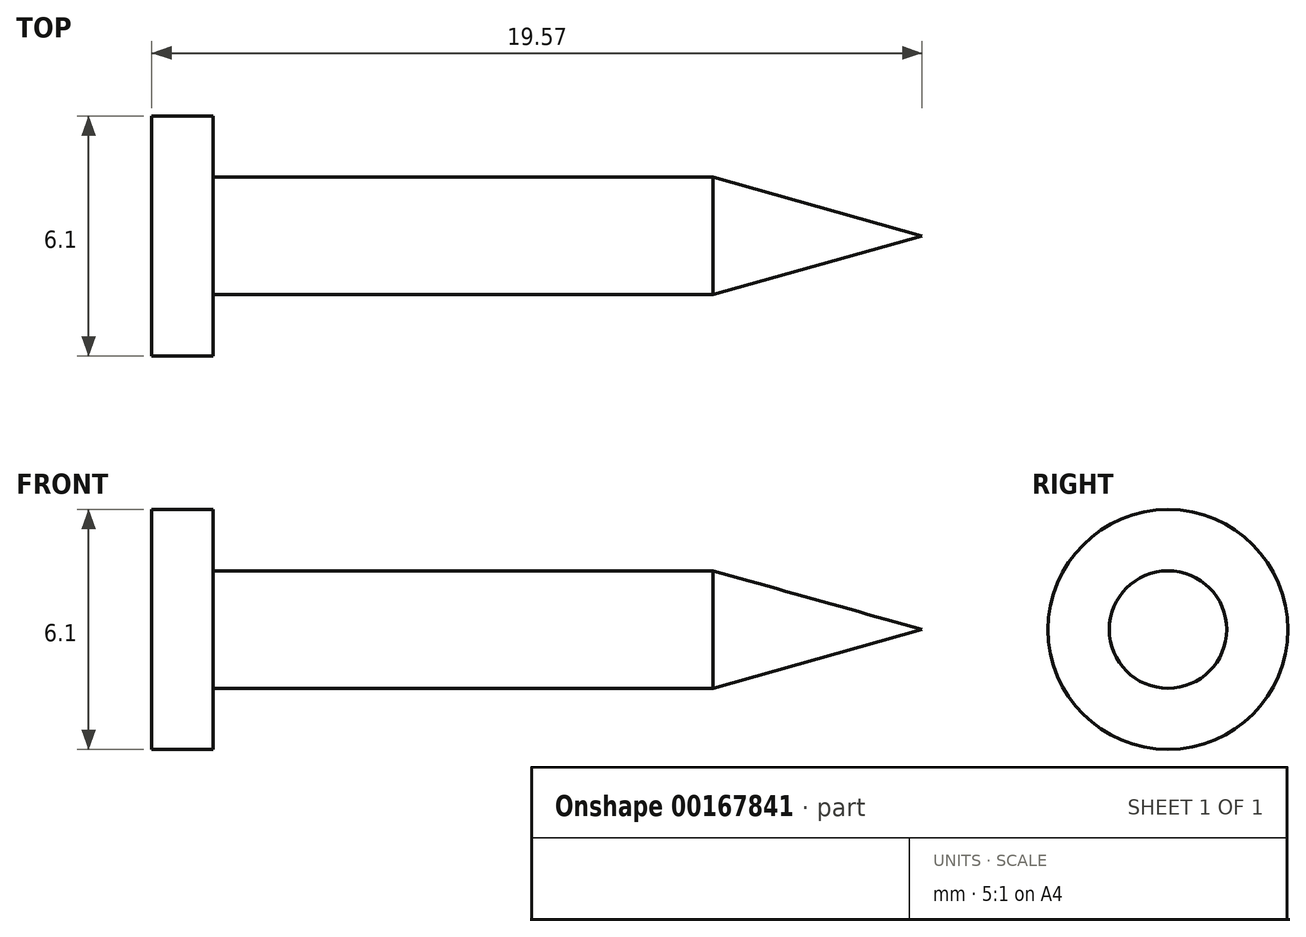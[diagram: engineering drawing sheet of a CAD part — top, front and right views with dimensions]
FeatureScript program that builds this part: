
annotation { "Feature Type Name" : "Feature", "Feature Type Description" : "" }
export const myFeature = defineFeature(function(context is Context, id is Id, definition is map)
    precondition{}
    {
        {
            var Q0;
            Q0=qCreatedBy(makeId("Front.planeOp"),FACE);
            var sketch = newSketch(context, id + "F0", { "sketchPlane" : qUnion([Q0])});
            skLineSegment(sketch, "E0", {"start": v(0, 0) * mm, "end": v(0, 3.05) * mm});
            skLineSegment(sketch, "E1", {"start": v(0, 3.05) * mm, "end": v(1.56, 3.05) * mm});
            skLineSegment(sketch, "E2", {"start": v(1.56, 3.05) * mm, "end": v(1.56, 1.5) * mm});
            skLineSegment(sketch, "E3", {"start": v(1.56, 1.5) * mm, "end": v(14.26, 1.5) * mm});
            skLineSegment(sketch, "E4", {"start": v(14.26, 1.5) * mm, "end": v(19.57, 0) * mm});
            skLineSegment(sketch, "E5", {"start": v(19.57, 0) * mm, "end": v(0, 0) * mm});
            skSolve(sketch);
        }
        {
            var Q0;
            Q0 = qSketchRegion(id + "F0", true);
            var Q1;
            Q1=sQuery(id+"F0.wireOp",EDGE,"E5");
            revolve(context, id + "F1", {"entities" : qUnion([Q0]), "axis" : qUnion([Q1]), "revolveType" : RevolveType.FULL});
        }
    });
